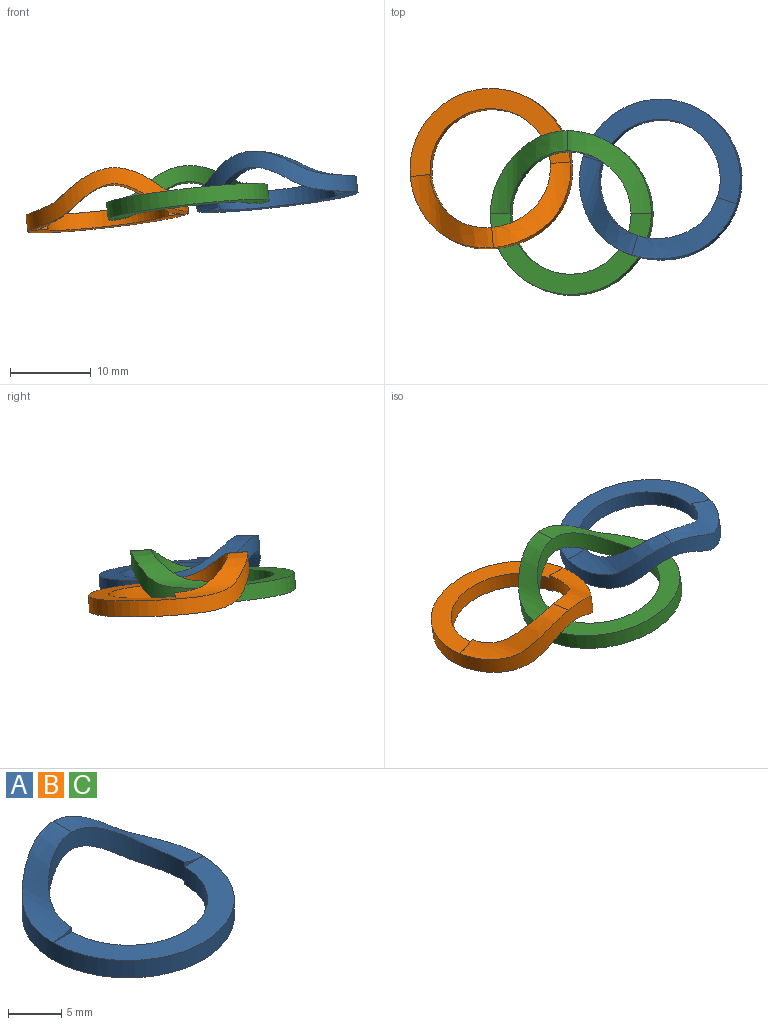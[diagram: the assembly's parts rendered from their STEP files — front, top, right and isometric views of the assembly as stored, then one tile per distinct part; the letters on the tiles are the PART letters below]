
ASSEMBLY  parts=3 mates=2
PART A: 12 faces, bbox 20x20x6 mm
  f0: plane 20x10mm, normal (0,0,-1), area 68.7mm2, adj f1,f4,f5,f6
  f1: plane 2.53x0.43mm, normal (0,1,0), area 0.4mm2, adj f0,f2,f6
  f2: extruded ~10x10mm, area 37.4mm2, adj f1,f3,f5,f6
  f3: extruded ~10x10mm, area 37.4mm2, adj f2,f4,f5,f6
  f4: plane 2.53x0.43mm, normal (0,1,0), area 0.4mm2, adj f0,f3,f6
  f5: cylinder r=10mm len=20mm, axis (0,0,-1), area 130.3mm2, adj f0,f2,f3,f7,f8,f11
  f6: cylinder r=7.5mm len=15mm, axis (0,0,-1), area 99.8mm2, adj f0,f1,f2,f3,f4,f7,f8,f9
  f7: extruded ~10x10mm, area 37.7mm2, adj f5,f6,f8,f10
  f8: extruded ~10x10mm, area 37.7mm2, adj f5,f6,f7,f9
  f9: plane 2.51x0.51mm, normal (0,-1,0), area 0.5mm2, adj f6,f8,f11
  f10: plane 2.51x0.51mm, normal (0,-1,0), area 0.5mm2, adj f6,f7,f11
  f11: plane 20x10mm, normal (0,0,1), area 68.7mm2, adj f5,f6,f9,f10
PART B: same geometry as A
PART C: same geometry as A
PLACE A rot(axis=(-0.06,0.02,1),162.6deg) t=(17.37,13.03,-1.86)mm
PLACE B rot(axis=(0.06,-0.04,-1),175deg) t=(-3.56,14.35,-4.37)mm
PLACE C rot(axis=(-0.5,-0.87,0),7.6deg) t=(6.38,8.86,-2.85)mm fixed
MATE planar B.f11 <-> C.f11  axis (-0.11,0.07,0.99) through (-4.25,20.06,-2.81)mm
MATE planar A.f11 <-> C.f11  axis (-0.11,0.07,0.99) through (18.82,18.51,-0.04)mm
